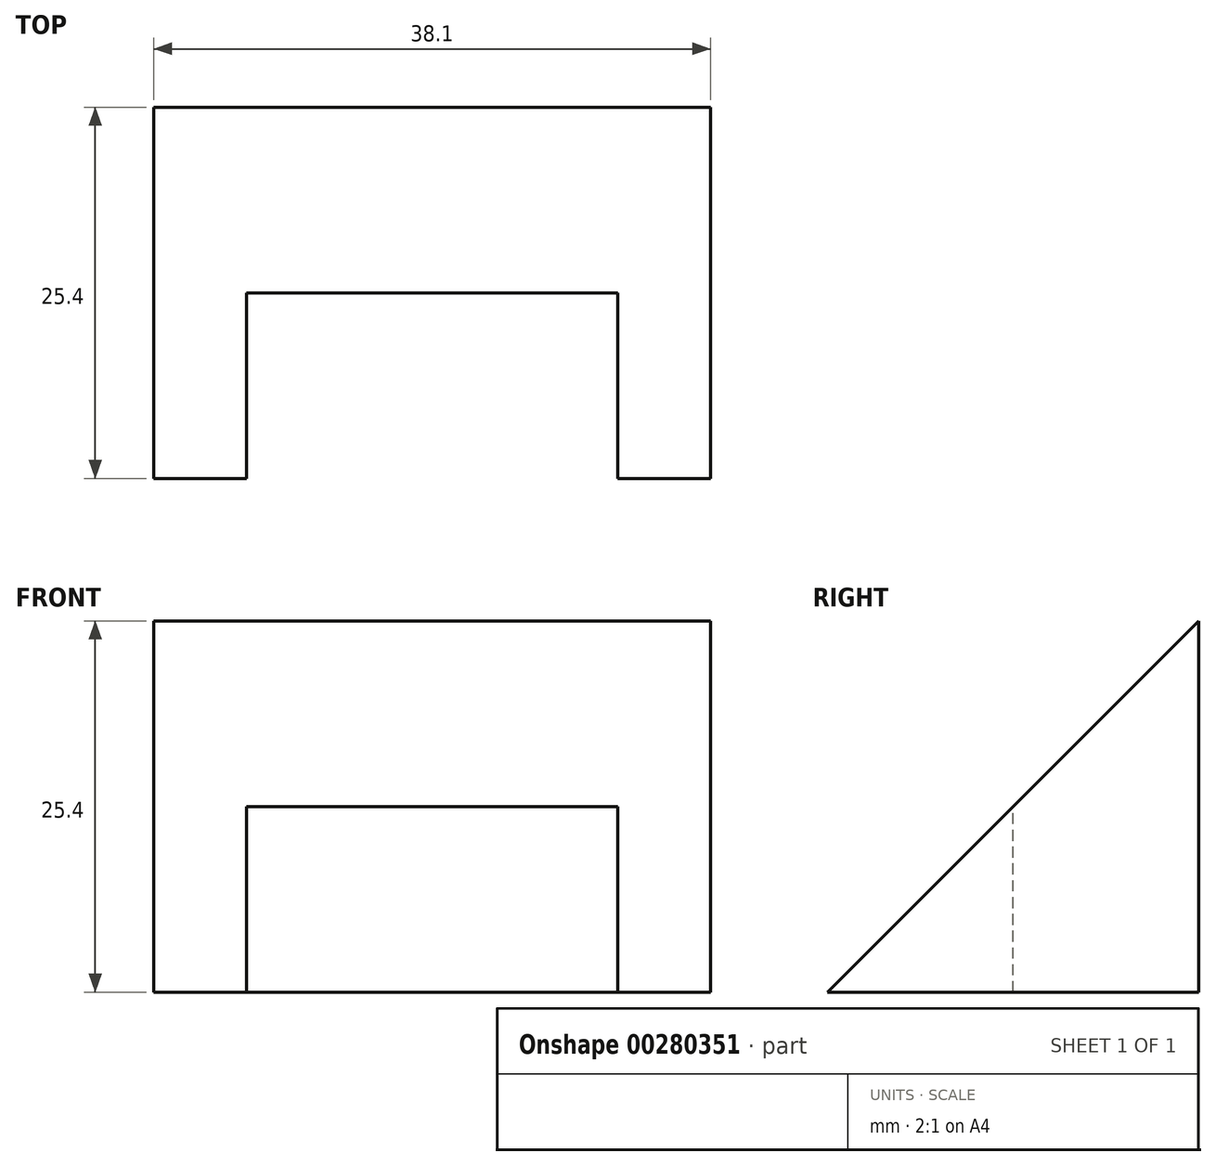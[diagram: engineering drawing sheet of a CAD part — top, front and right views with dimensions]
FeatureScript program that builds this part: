
annotation { "Feature Type Name" : "Feature", "Feature Type Description" : "" }
export const myFeature = defineFeature(function(context is Context, id is Id, definition is map)
    precondition{}
    {
        {
            var Q0;
            Q0=qCreatedBy(makeId("Top.planeOp"),FACE);
            var sketch = newSketch(context, id + "F0", { "sketchPlane" : qUnion([Q0])});
            skLineSegment(sketch, "E0.bottom", {"start": v(0, 0) * mm, "end": v(38.1, 0) * mm});
            skLineSegment(sketch, "E0.top", {"start": v(0, 25.4) * mm, "end": v(38.1, 25.4) * mm});
            skLineSegment(sketch, "E0.left", {"start": v(0, 0) * mm, "end": v(0, 25.4) * mm});
            skLineSegment(sketch, "E0.right", {"start": v(38.1, 0) * mm, "end": v(38.1, 25.4) * mm});
            skSolve(sketch);
        }
        {
            var Q0;
            Q0 = qSketchRegion(id + "F0", true);
            extrude(context, id + "F1", {"entities" : qUnion([Q0]), "depth" : 25.4 * mm});
        }
        {
            var Q0;
            Q0=makeQuery(id+"F1.opExtrude","CAP_FACE",FACE,{"disambiguationData":[OSD([sQuery(id+"F0.wireOp",EDGE,"E0.bottom"),sQuery(id+"F0.wireOp",EDGE,"E0.top"),sQuery(id+"F0.wireOp",EDGE,"E0.left"),sQuery(id+"F0.wireOp",EDGE,"E0.right")])],"isStart":false});
            var sketch = newSketch(context, id + "F2", { "sketchPlane" : qUnion([Q0])});
            skLineSegment(sketch, "E1.bottom", {"start": v(6.35, 0) * mm, "end": v(31.75, 0) * mm});
            skLineSegment(sketch, "E1.top", {"start": v(6.35, 12.7) * mm, "end": v(31.75, 12.7) * mm});
            skLineSegment(sketch, "E1.left", {"start": v(6.35, 0) * mm, "end": v(6.35, 12.7) * mm});
            skLineSegment(sketch, "E1.right", {"start": v(31.75, 0) * mm, "end": v(31.75, 12.7) * mm});
            skSolve(sketch);
        }
        {
            var Q0;
            Q0 = qSketchRegion(id + "F2", true);
            extrude(context, id + "F3", {"entities" : qUnion([Q0]), "operationType" : NewBodyOperationType.REMOVE, "oppositeDirection" : true, "depth" : 25.4 * mm});
        }
        {
            var Q0;
            Q0=makeQuery(id+"F1.opExtrude","SWEPT_FACE",FACE,{"disambiguationData":[OSD([sQuery(id+"F0.wireOp",EDGE,"E0.right")])]});
            var sketch = newSketch(context, id + "F4", { "sketchPlane" : qUnion([Q0])});
            skLineSegment(sketch, "E2", {"start": v(0, 0) * mm, "end": v(25.4, 25.4) * mm});
            skSolve(sketch);
        }
        {
            var Q0;
            Q0=makeQuery(id+"F4.imprint","IMPRINT",FACE,{"disambiguationData":[TD([[makeQuery(id+"F4.imprint","IMPRINT",EDGE,{"derivedFrom":sQuery(id+"F4.wireOp",EDGE,"E2")}),1.0]])]});
            extrude(context, id + "F5", {"entities" : qUnion([Q0]), "operationType" : NewBodyOperationType.REMOVE, "oppositeDirection" : true, "depth" : 38.1 * mm});
        }
    });
